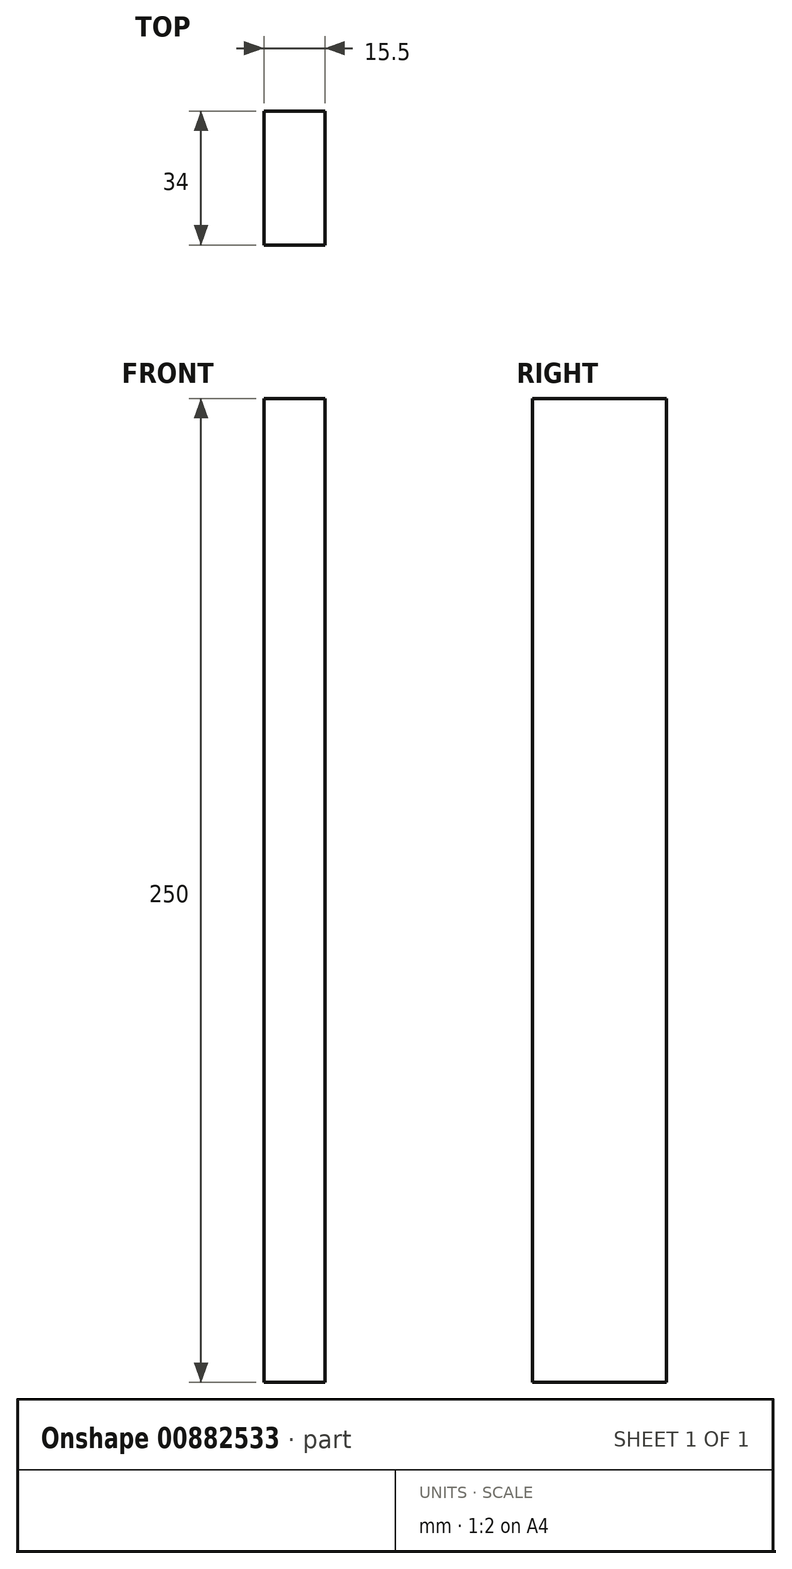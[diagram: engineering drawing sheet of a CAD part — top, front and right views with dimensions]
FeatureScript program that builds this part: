
annotation { "Feature Type Name" : "Feature", "Feature Type Description" : "" }
export const myFeature = defineFeature(function(context is Context, id is Id, definition is map)
    precondition{}
    {
        {
            var Q0;
            Q0=qCreatedBy(makeId("Top.planeOp"),FACE);
            var sketch = newSketch(context, id + "F0", { "sketchPlane" : qUnion([Q0])});
            skLineSegment(sketch, "E0.bottom", {"start": v(0, 0) * mm, "end": v(15.5, 0) * mm});
            skLineSegment(sketch, "E0.top", {"start": v(0, -34) * mm, "end": v(15.5, -34) * mm});
            skLineSegment(sketch, "E0.left", {"start": v(0, 0) * mm, "end": v(0, -34) * mm});
            skLineSegment(sketch, "E0.right", {"start": v(15.5, 0) * mm, "end": v(15.5, -34) * mm});
            skSolve(sketch);
        }
        {
            var Q0;
            Q0=qSketchRegion(id+"F0",true);
            extrude(context, id + "F1", {"entities" : qUnion([Q0]), "depth" : 250 * mm, "offsetDistance" : 25 * mm});
        }
    });
